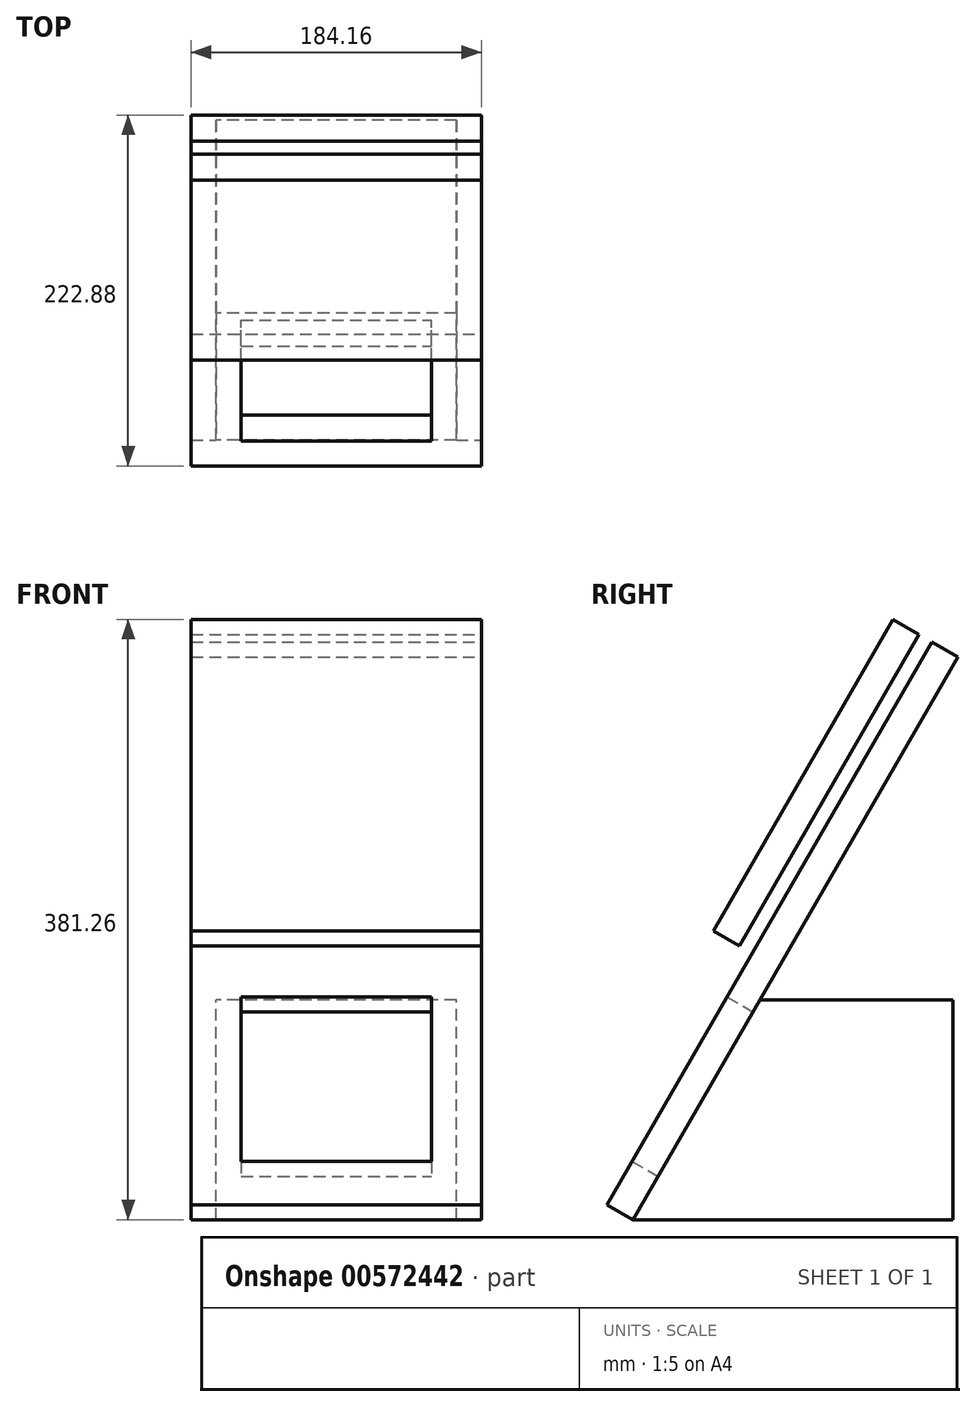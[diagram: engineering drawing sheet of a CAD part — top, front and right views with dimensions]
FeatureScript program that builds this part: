
annotation { "Feature Type Name" : "Feature", "Feature Type Description" : "" }
export const myFeature = defineFeature(function(context is Context, id is Id, definition is map)
    precondition{}
    {
        {
            var Q0;
            Q0=qCreatedBy(makeId("Right.planeOp"),FACE);
            var sketch = newSketch(context, id + "F0", { "sketchPlane" : qUnion([Q0])});
            skLineSegment(sketch, "E0", {"start": v(0, 0) * mm, "end": v(203.2, 0) * mm});
            skLineSegment(sketch, "E1", {"start": v(203.2, 0) * mm, "end": v(203.2, 139.7) * mm});
            skLineSegment(sketch, "E2", {"start": v(203.2, 139.7) * mm, "end": v(80.66, 139.7) * mm});
            skLineSegment(sketch, "E3", {"start": v(80.66, 139.7) * mm, "end": v(0, 0) * mm});
            skSolve(sketch);
        }
        {
            var Q0;
            Q0=makeQuery(id+"F0.imprint","IMPRINT",FACE,{"disambiguationData":[TD([[makeQuery(id+"F0.imprint","IMPRINT",EDGE,{"derivedFrom":sQuery(id+"F0.wireOp",EDGE,"E0")}),1.0]])]});
            extrude(context, id + "F1", {"entities" : qUnion([Q0]), "depth" : 152.4 * mm, "offsetDistance" : 25.4 * mm});
        }
        {
            var Q0;
            Q0=makeQuery(id+"F1.opExtrude","SWEPT_FACE",FACE,{"disambiguationData":[OSD([sQuery(id+"F0.wireOp",EDGE,"E3")])]});
            var sketch = newSketch(context, id + "F2", { "sketchPlane" : qUnion([Q0])});
            skLineSegment(sketch, "E4.bottom", {"start": v(76.2, 0) * mm, "end": v(168.28, 0) * mm});
            skLineSegment(sketch, "E4.top", {"start": v(76.2, 412.75) * mm, "end": v(168.28, 412.75) * mm});
            skLineSegment(sketch, "E4.right", {"start": v(168.28, 0) * mm, "end": v(168.28, 412.75) * mm});
            skLineSegment(sketch, "E5.MirrorCS", {"start": v(76.2, 412.75) * mm, "end": v(-15.87, 412.75) * mm});
            skLineSegment(sketch, "E6.MirrorCS", {"start": v(-15.87, 0) * mm, "end": v(-15.87, 412.75) * mm});
            skLineSegment(sketch, "E7.MirrorCS", {"start": v(76.2, 0) * mm, "end": v(-15.87, 0) * mm});
            skLineSegment(sketch, "E8", {"start": v(-15.87, 0) * mm, "end": v(-15.87, 31.75) * mm, "construction": true});
            skLineSegment(sketch, "E9", {"start": v(-15.87, 31.75) * mm, "end": v(15.88, 31.75) * mm, "construction": true});
            skLineSegment(sketch, "E10.bottom", {"start": v(15.88, 31.75) * mm, "end": v(136.53, 31.75) * mm});
            skLineSegment(sketch, "E10.top", {"start": v(15.88, 152.4) * mm, "end": v(136.53, 152.4) * mm});
            skLineSegment(sketch, "E10.left", {"start": v(15.88, 31.75) * mm, "end": v(15.88, 152.4) * mm});
            skLineSegment(sketch, "E10.right", {"start": v(136.53, 31.75) * mm, "end": v(136.53, 152.4) * mm});
            skSolve(sketch);
        }
        {
            var Q0;
            Q0 = qSketchRegion(id + "F2", true);
            extrude(context, id + "F3", {"entities" : qUnion([Q0]), "operationType" : NewBodyOperationType.ADD, "depth" : 19.05 * mm, "offsetDistance" : 25.4 * mm});
        }
        {
            var Q0;
            Q0=makeQuery(id+"F3.opExtrude","CAP_FACE",FACE,{"disambiguationData":[OSD([sQuery(id+"F2.wireOp",EDGE,"E4.bottom"),sQuery(id+"F2.wireOp",EDGE,"E4.top"),sQuery(id+"F2.wireOp",EDGE,"E4.right"),sQuery(id+"F2.wireOp",EDGE,"E5.MirrorCS"),sQuery(id+"F2.wireOp",EDGE,"E6.MirrorCS"),sQuery(id+"F2.wireOp",EDGE,"E7.MirrorCS"),sQuery(id+"F2.wireOp",EDGE,"E10.bottom"),sQuery(id+"F2.wireOp",EDGE,"E10.top"),sQuery(id+"F2.wireOp",EDGE,"E10.left"),sQuery(id+"F2.wireOp",EDGE,"E10.right")])],"isStart":false});
            cPlane(context, id + "F4", {"entities" : qUnion([Q0]), "cplaneType" : CPlaneType.OFFSET, "offset" : 9.52 * mm, "width" : 152.4 * mm, "height" : 152.4 * mm});
        }
        {
            var Q0;
            Q0=qCreatedBy(id+"F4.planeOp",FACE);
            var sketch = newSketch(context, id + "F5", { "sketchPlane" : qUnion([Q0])});
            skLineSegment(sketch, "E11.bottom", {"start": v(-15.87, 412.75) * mm, "end": v(168.28, 412.75) * mm});
            skLineSegment(sketch, "E11.top", {"start": v(-15.87, 184.15) * mm, "end": v(168.28, 184.15) * mm});
            skLineSegment(sketch, "E11.left", {"start": v(-15.87, 412.75) * mm, "end": v(-15.87, 184.15) * mm});
            skLineSegment(sketch, "E11.right", {"start": v(168.28, 412.75) * mm, "end": v(168.28, 184.15) * mm});
            skSolve(sketch);
        }
        {
            var Q0;
            Q0 = qSketchRegion(id + "F5", true);
            extrude(context, id + "F6", {"entities" : qUnion([Q0]), "depth" : 19.05 * mm, "offsetDistance" : 25.4 * mm});
        }
    });
